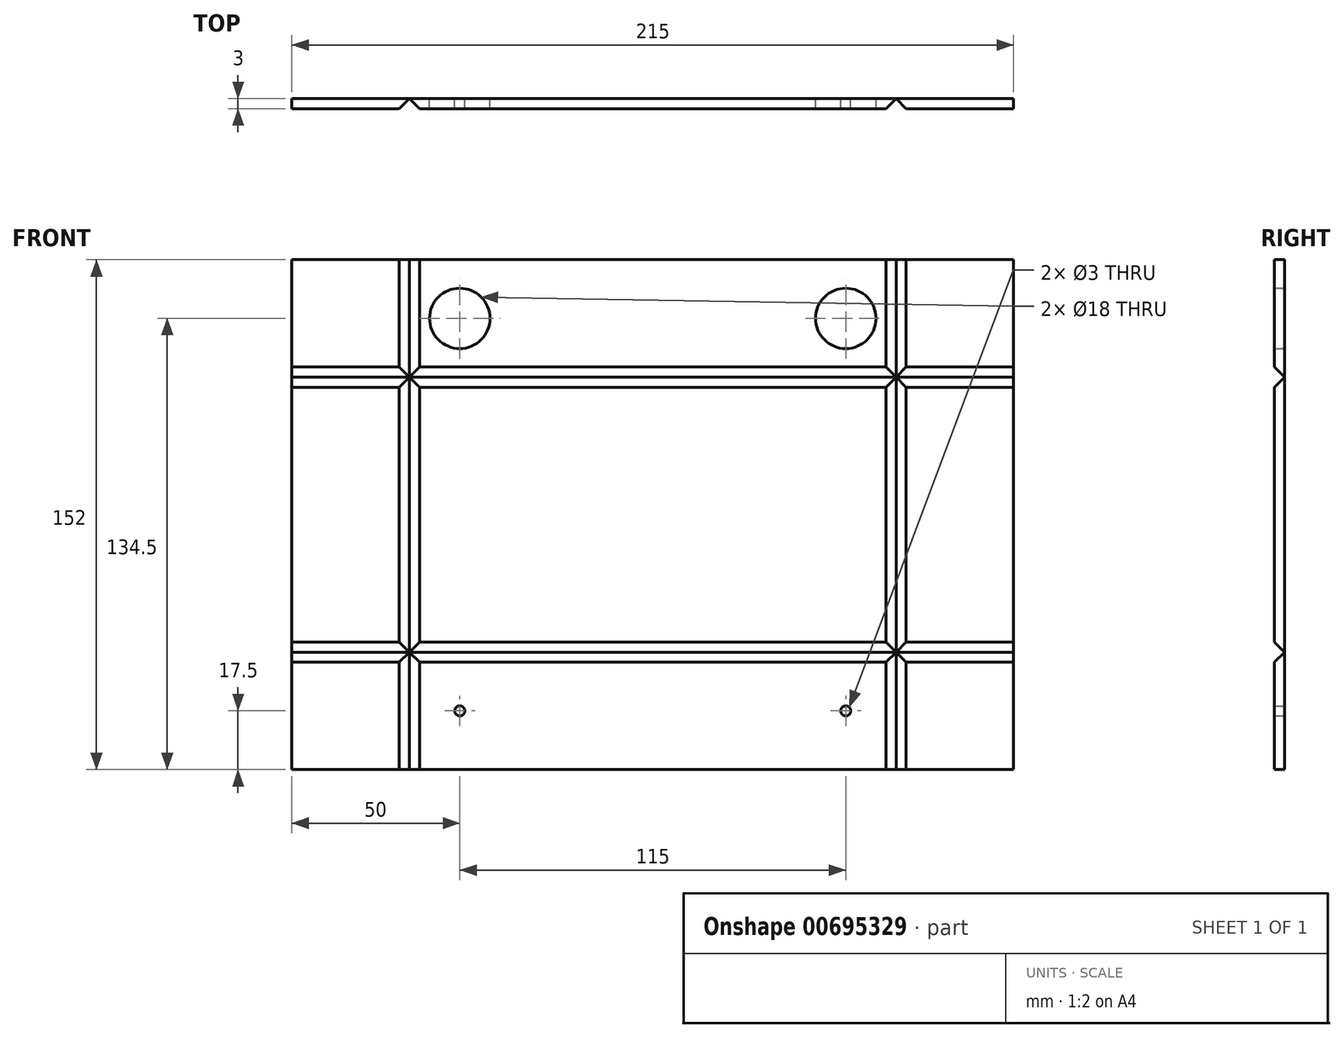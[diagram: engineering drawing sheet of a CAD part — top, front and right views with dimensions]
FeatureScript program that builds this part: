
annotation { "Feature Type Name" : "Feature", "Feature Type Description" : "" }
export const myFeature = defineFeature(function(context is Context, id is Id, definition is map)
    precondition{}
    {
        {
            var Q0;
            Q0=qCreatedBy(makeId("Front.planeOp"),FACE);
            var sketch = newSketch(context, id + "F0", { "sketchPlane" : qUnion([Q0])});
            skLineSegment(sketch, "E0.bottom", {"start": v(107.5, 76) * mm, "end": v(-107.5, 76) * mm});
            skLineSegment(sketch, "E0.top", {"start": v(107.5, -76) * mm, "end": v(-107.5, -76) * mm});
            skLineSegment(sketch, "E0.left", {"start": v(107.5, 76) * mm, "end": v(107.5, -76) * mm});
            skLineSegment(sketch, "E0.right", {"start": v(-107.5, 76) * mm, "end": v(-107.5, -76) * mm});
            skPoint(sketch, "E0.middle", {"position": v(0, 0) * mm});
            skSolve(sketch);
        }
        {
            var Q0;
            Q0 = qSketchRegion(id + "F0", true);
            extrude(context, id + "F1", {"entities" : qUnion([Q0]), "depth" : 3 * mm, "offsetDistance" : 25 * mm});
        }
        {
            var Q0;
            Q0=makeQuery(id+"F1.opExtrude","SWEPT_FACE",FACE,{"disambiguationData":[OSD([sQuery(id+"F0.wireOp",EDGE,"E0.top")])]});
            var sketch = newSketch(context, id + "F2", { "sketchPlane" : qUnion([Q0])});
            skLineSegment(sketch, "E1", {"start": v(-107.5, 0) * mm, "end": v(-72.5, 0) * mm, "construction": true});
            skLineSegment(sketch, "E2", {"start": v(107.5, 0) * mm, "end": v(72.5, 0) * mm, "construction": true});
            skLineSegment(sketch, "E3", {"start": v(72.5, 0) * mm, "end": v(72.5, 3) * mm, "construction": true});
            skLineSegment(sketch, "E4", {"start": v(-72.5, 0) * mm, "end": v(-72.5, 3) * mm, "construction": true});
            skLineSegment(sketch, "E5", {"start": v(-72.5, 0) * mm, "end": v(-69.5, 3) * mm});
            skLineSegment(sketch, "E6", {"start": v(-72.5, 0) * mm, "end": v(-75.5, 3) * mm});
            skLineSegment(sketch, "E7", {"start": v(-75.5, 3) * mm, "end": v(-69.5, 3) * mm});
            skLineSegment(sketch, "E8", {"start": v(72.5, 0) * mm, "end": v(75.5, 3) * mm});
            skLineSegment(sketch, "E9", {"start": v(75.5, 3) * mm, "end": v(69.5, 3) * mm});
            skLineSegment(sketch, "E10", {"start": v(69.5, 3) * mm, "end": v(72.5, 0) * mm});
            skSolve(sketch);
        }
        {
            var Q0;
            Q0 = qSketchRegion(id + "F2", true);
            extrude(context, id + "F3", {"entities" : qUnion([Q0]), "operationType" : NewBodyOperationType.REMOVE, "oppositeDirection" : true, "depth" : 174.7 * mm, "offsetDistance" : 25 * mm});
        }
        {
            var Q0;
            Q0=makeQuery(id+"F1.opExtrude","SWEPT_FACE",FACE,{"disambiguationData":[OSD([sQuery(id+"F0.wireOp",EDGE,"E0.right")])]});
            var sketch = newSketch(context, id + "F4", { "sketchPlane" : qUnion([Q0])});
            skLineSegment(sketch, "E11", {"start": v(0, 76) * mm, "end": v(0, 41) * mm, "construction": true});
            skLineSegment(sketch, "E12", {"start": v(0, 41) * mm, "end": v(3, 41) * mm, "construction": true});
            skLineSegment(sketch, "E13", {"start": v(0, -76) * mm, "end": v(0, -41) * mm, "construction": true});
            skLineSegment(sketch, "E14", {"start": v(0, -41) * mm, "end": v(3, -41) * mm, "construction": true});
            skLineSegment(sketch, "E15", {"start": v(0, 41) * mm, "end": v(3, 38) * mm});
            skLineSegment(sketch, "E16", {"start": v(3, 38) * mm, "end": v(3, 44) * mm});
            skLineSegment(sketch, "E17", {"start": v(3, 44) * mm, "end": v(0, 41) * mm});
            skLineSegment(sketch, "E18", {"start": v(0, -41) * mm, "end": v(3, -44) * mm});
            skLineSegment(sketch, "E19", {"start": v(3, -44) * mm, "end": v(3, -38) * mm});
            skLineSegment(sketch, "E20", {"start": v(3, -38) * mm, "end": v(0, -41) * mm});
            skSolve(sketch);
        }
        {
            var Q0;
            Q0 = qSketchRegion(id + "F4", true);
            extrude(context, id + "F5", {"entities" : qUnion([Q0]), "operationType" : NewBodyOperationType.REMOVE, "oppositeDirection" : true, "depth" : 226.7 * mm, "offsetDistance" : 25 * mm});
        }
        {
            var Q0;
            {var subQ0=sQuery(id+"F0.wireOp",EDGE,"E0.bottom");var subQ1=makeQuery(id+"F1.opExtrude","SWEPT_FACE",FACE,{"disambiguationData":[OSD([subQ0])]});var subQ2=makeQuery(id+"F3.opExtrude","SWEPT_FACE",FACE,{"disambiguationData":[OSD([sQuery(id+"F2.wireOp",EDGE,"E5")])]});var subQ4=sQuery(id+"F0.wireOp",EDGE,"E0.top");Q0=makeQuery(id+"F5.boolean.opBoolean","SPLIT",FACE,{"disambiguationData":[TD([subQ1])],"derivedFrom":makeQuery(id+"F3.boolean.opBoolean","SPLIT",FACE,{"disambiguationData":[TD([subQ2])],"derivedFrom":makeQuery(id+"F1.opExtrude","CAP_FACE",FACE,{"disambiguationData":[OSD([subQ0,subQ4,sQuery(id+"F0.wireOp",EDGE,"E0.left"),sQuery(id+"F0.wireOp",EDGE,"E0.right")])],"isStart":true})})});}
            var sketch = newSketch(context, id + "F6", { "sketchPlane" : qUnion([Q0])});
            skCircle(sketch, "E21", {"center": v(-57.5, 58.5) * mm, "radius": 9 * mm});
            skCircle(sketch, "E22", {"center": v(57.5, 58.5) * mm, "radius": 9 * mm});
            skLineSegment(sketch, "E23", {"start": v(0, 76) * mm, "end": v(0, 41) * mm, "construction": true});
            skLineSegment(sketch, "E24", {"start": v(0, 58.5) * mm, "end": v(-72.5, 58.5) * mm, "construction": true});
            skCircle(sketch, "E25", {"center": v(-57.5, -58.5) * mm, "radius": 1.5 * mm});
            skCircle(sketch, "E26", {"center": v(57.5, -58.5) * mm, "radius": 1.5 * mm});
            skSolve(sketch);
        }
        {
            var Q0;
            Q0 = qSketchRegion(id + "F6", true);
            extrude(context, id + "F7", {"entities" : qUnion([Q0]), "operationType" : NewBodyOperationType.REMOVE, "oppositeDirection" : true, "depth" : 25 * mm, "offsetDistance" : 25 * mm});
        }
    });
